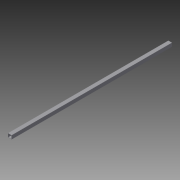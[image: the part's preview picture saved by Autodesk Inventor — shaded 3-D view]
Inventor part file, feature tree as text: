
AUTODESK INVENTOR PART (.ipt)
format: ipt  version: 2013 (Build 170138000, 138)  size: 72,192 bytes
history: native  units: in
note: dims shown in document units (in); Inventor stores cm internally (conversion verified against a paired STEP export)
features: other x3, sketch x1
ambient origin geometry x8: Origin, YZ Plane, XZ Plane, XY Plane, X Axis, Y Axis, Z Axis, Center Point
bodies: Solid1 (feature_tree)
feature tree (4):
  other  "Frame0002.ipt"
  other  "Solid1::Frame0002.ipt"
  other  "TaggingFeature1"
  sketch  "Sketch1"  dims[d0=0.3937in d1=1.75in d2=0.125in d3=78.0in d4=0.0in]
